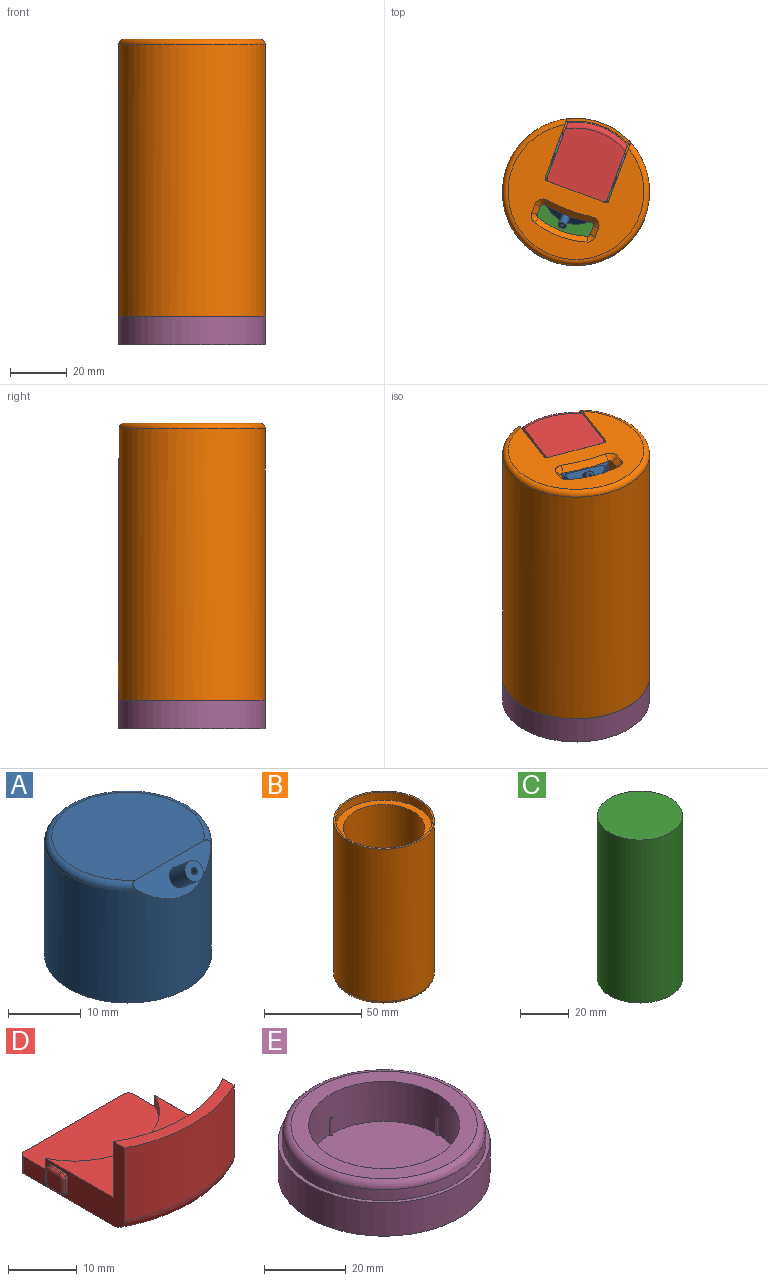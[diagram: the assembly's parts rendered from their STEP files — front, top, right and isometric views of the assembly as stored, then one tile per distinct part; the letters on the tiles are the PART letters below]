
ASSEMBLY  parts=5 mates=5
PART A: 32 faces, bbox 24.9x26.3x21.7 mm
  f0: cylinder r=1.6mm len=8mm, axis (0,0,-1), area 62.1mm2, adj f7,f15,f16,f17,f18,f19,f28
  f1: cylinder r=10.5mm len=21mm, axis (0,0,-1), area 1198.2mm2, adj f2,f3,f10,f12,f13,f20,f21,f22
  f2: plane 18.13x9.5mm, normal (0,0,-1), area 130.4mm2, adj f1,f6,f13,f21,f26
  f3: plane 5.66x3.24mm, normal (0,0.77,-0.64), area 15.1mm2, adj f1,f12,f25
  f4: cylinder r=1.5mm len=3.46mm, axis (0,-0.77,0.64), area 10.5mm2, adj f5,f6,f23,f24,f27
  f5: cylinder r=3mm len=0.33mm, axis (0,0,1), area 0mm2, adj f4,f6,f24
  f6: cylinder r=3mm len=15mm, axis (0,0,1), area 246.3mm2, adj f2,f4,f5,f12,f14,f20,f21,f22
  f7: plane 2x0.35mm, normal (0,0,-1), area 0.5mm2, adj f0,f18
  f8: cylinder r=11.5mm len=23mm, axis (0,0,-1), area 1342.1mm2, adj f10,f11,f29
  f9: plane 21x18.64mm, normal (0,0,1), area 325mm2, adj f11,f29
  f10: plane 23x23mm, normal (0,0,-1), area 69.1mm2, adj f1,f8
  f11: plane 14.95x4mm, normal (0,-0.77,0.64), area 50.5mm2, adj f8,f9,f29,f30
  f12: plane 18.13x9.5mm, normal (0,0,-1), area 130.4mm2, adj f1,f3,f6,f20,f25
  f13: plane 5.66x3.24mm, normal (0,0.77,-0.64), area 15.1mm2, adj f1,f2,f26
  f14: plane 6x6mm, normal (0,0,-1), area 7mm2, adj f6,f16
  f15: plane 2x0.35mm, normal (0,0,-1), area 0.5mm2, adj f0,f17
  f16: cone r=1.6mm half-angle=45deg, axis (0,0,-1), area 18.7mm2, adj f0,f14
  f17: plane 4x2mm, normal (-1,0,0), area 8mm2, adj f0,f15,f19
  f18: plane 4x2mm, normal (1,0,0), area 8mm2, adj f0,f7,f19
  f19: plane 3.2x2.5mm, normal (0,0,-1), area 7.1mm2, adj f0,f17,f18
  f20: plane 7.62x5mm, normal (-1,0,0), area 38.1mm2, adj f1,f6,f12,f22
  f21: plane 7.62x5mm, normal (1,0,0), area 38.1mm2, adj f1,f2,f6,f22
  f22: plane 7.67x2mm, normal (0,0,-1), area 15.1mm2, adj f1,f6,f20,f21
  f23: plane 0.4x0.02mm, normal (0,0,-1), area 0mm2, adj f4,f6,f25
  f24: plane 0.4x0.02mm, normal (0,0,-1), area 0mm2, adj f4,f5,f26
  f25: plane 7.79x6.72mm, normal (-1,0,0), area 48mm2, adj f1,f3,f6,f12,f23,f27
  f26: plane 7.79x6.72mm, normal (1,0,0), area 48mm2, adj f1,f2,f6,f13,f24,f27
  f27: plane 7.5x3mm, normal (0,0,-1), area 16.9mm2, adj f1,f4,f25,f26
  f28: cylinder r=0.5mm len=12.25mm, axis (0,-0.77,0.64), area 46.4mm2, adj f0,f31
  f29: torus R=10.5mm, axis (0,0,1), area 85.1mm2, adj f8,f9,f11
  f30: cylinder r=1.5mm len=4.99mm, axis (0,0.77,-0.64), area 37.7mm2, adj f11,f31
  f31: plane 3x2.3mm, normal (0,-0.77,0.64), area 6.3mm2, adj f28,f30
PART B: 56 faces, bbox 56.3x54.1x98 mm
  f0: plane 42x36.65mm, normal (0,0,1), area 733.9mm2, adj f1,f10,f11,f12,f16,f19,f29,f31
  f1: cylinder r=21mm len=91mm, axis (0,0,1), area 11675.7mm2, adj f0,f2,f8,f16,f17,f29,f30,f46
  f2: plane 22x4.11mm, normal (0,0,-1), area 23.1mm2, adj f1,f14,f46,f47
  f3: cylinder r=26mm len=96mm, axis (0,0,-1), area 15408.9mm2, adj f4,f6,f9,f10,f11,f42,f43
  f4: torus R=24mm, axis (0,0,1), area 420.3mm2, adj f3,f5,f10,f11
  f5: plane 48x44.78mm, normal (0,0,-1), area 1037.7mm2, adj f4,f10,f11,f12,f44,f45,f48,f49
  f6: plane 52x52mm, normal (0,0,1), area 160.2mm2, adj f3,f7
  f7: cylinder r=25mm len=50mm, axis (0,0,1), area 785.4mm2, adj f6,f8
  f8: plane 50x50mm, normal (0,0,1), area 578.1mm2, adj f1,f7
  f9: plane 22x3.55mm, normal (0,0,-1), area 22.7mm2, adj f3,f13,f42,f43
  f10: plane 23.07x18mm, normal (-1,0,0), area 253.9mm2, adj f0,f3,f4,f5,f13,f14,f15,f30
  f11: plane 23.07x18mm, normal (1,0,0), area 253.9mm2, adj f0,f3,f4,f5,f13,f14,f15,f17
  f12: plane 22x2mm, normal (0,1,0), area 44mm2, adj f0,f5,f44,f45
  f13: cylinder r=25mm len=24mm, axis (0,0,-1), area 125.7mm2, adj f9,f10,f11,f15,f42,f43
  f14: cylinder r=22mm len=24mm, axis (0,0,-1), area 127.4mm2, adj f2,f10,f11,f15,f46,f47
  f15: plane 24x6.56mm, normal (0,0,-1), area 75.6mm2, adj f10,f11,f13,f14
  f16: plane 15.65x10mm, normal (-1,0,0), area 142.8mm2, adj f0,f1,f17,f18,f19
  f17: plane 9.23x2mm, normal (0,0,1), area 17mm2, adj f1,f11,f16,f18
  f18: cylinder r=8mm len=8mm, axis (1,0,0), area 25.1mm2, adj f11,f16,f17,f19
  f19: plane 2x2mm, normal (0,-1,0), area 4mm2, adj f0,f11,f16,f18
  f20: plane 2x0.5mm, normal (0,0,-1), area 1mm2, adj f11,f21,f27,f28
  f21: cylinder r=1mm len=1mm, axis (1,0,0), area 0.8mm2, adj f11,f20,f22,f28
  f22: plane 5x0.5mm, normal (0,1,0), area 2.5mm2, adj f11,f21,f23,f28
  f23: cylinder r=1mm len=1mm, axis (1,0,0), area 0.8mm2, adj f11,f22,f24,f28
  f24: plane 2x0.5mm, normal (0,0,1), area 1mm2, adj f11,f23,f25,f28
  f25: cylinder r=1mm len=1mm, axis (1,0,0), area 0.8mm2, adj f11,f24,f26,f28
  f26: plane 5x0.5mm, normal (0,-1,0), area 2.5mm2, adj f11,f25,f27,f28
  f27: cylinder r=1mm len=1mm, axis (1,0,0), area 0.8mm2, adj f11,f20,f26,f28
  f28: plane 7x4mm, normal (1,0,0), area 27.1mm2, adj f20,f21,f22,f23,f24,f25,f26,f27
  f29: plane 15.65x10mm, normal (1,0,0), area 142.8mm2, adj f0,f1,f30,f31,f32
  f30: plane 9.23x2mm, normal (0,0,1), area 17mm2, adj f1,f10,f29,f32
  f31: plane 2x2mm, normal (0,-1,0), area 4mm2, adj f0,f10,f29,f32
  f32: cylinder r=8mm len=8mm, axis (-1,0,0), area 25.1mm2, adj f10,f29,f30,f31
  f33: plane 2x0.5mm, normal (0,0,-1), area 1mm2, adj f10,f34,f40,f41
  f34: cylinder r=1mm len=1mm, axis (-1,0,0), area 0.8mm2, adj f10,f33,f35,f41
  f35: plane 5x0.5mm, normal (0,-1,0), area 2.5mm2, adj f10,f34,f36,f41
  f36: cylinder r=1mm len=1mm, axis (-1,0,0), area 0.8mm2, adj f10,f35,f37,f41
  f37: plane 2x0.5mm, normal (0,0,1), area 1mm2, adj f10,f36,f38,f41
  f38: cylinder r=1mm len=1mm, axis (-1,0,0), area 0.8mm2, adj f10,f37,f39,f41
  f39: plane 5x0.5mm, normal (0,1,0), area 2.5mm2, adj f10,f38,f40,f41
  f40: cylinder r=1mm len=1mm, axis (-1,0,0), area 0.8mm2, adj f10,f33,f39,f41
  f41: plane 7x4mm, normal (-1,0,0), area 27.1mm2, adj f33,f34,f35,f36,f37,f38,f39,f40
  f42: cylinder r=1mm len=1.63mm, axis (0,1,0), area 1.8mm2, adj f3,f9,f11,f13
  f43: cylinder r=1mm len=1.63mm, axis (0,-1,0), area 1.8mm2, adj f3,f9,f10,f13
  f44: cylinder r=1mm len=2mm, axis (0,0,-1), area 3.1mm2, adj f0,f5,f11,f12
  f45: cylinder r=1mm len=2mm, axis (0,0,1), area 3.1mm2, adj f0,f5,f10,f12
  f46: cylinder r=1mm len=1.82mm, axis (0,-1,0), area 1.9mm2, adj f1,f2,f10,f14
  f47: cylinder r=1mm len=1.82mm, axis (0,1,0), area 1.9mm2, adj f1,f2,f11,f14
  f48: cone r=30mm half-angle=45deg, axis (0,0,-1), area 55.3mm2, adj f0,f5,f49,f50
  f49: cone r=1mm half-angle=45deg, axis (0,0,-1), area 7.1mm2, adj f0,f5,f48,f51
  f50: cone r=1mm half-angle=45deg, axis (0,0,-1), area 7.1mm2, adj f0,f5,f48,f52
  f51: plane 3.11x2mm, normal (-0.71,0,-0.71), area 8.8mm2, adj f0,f5,f49,f53
  f52: plane 3.11x2mm, normal (0.71,0,-0.71), area 8.8mm2, adj f0,f5,f50,f54
  f53: cone r=1mm half-angle=45deg, axis (0,0,-1), area 9.7mm2, adj f0,f5,f51,f55
  f54: cone r=1mm half-angle=45deg, axis (0,0,-1), area 9.7mm2, adj f0,f5,f52,f55
  f55: cone r=58mm half-angle=45deg, axis (0,0,1), area 49.4mm2, adj f0,f5,f53,f54
PART C: 3 faces, bbox 35x35x82 mm
  f0: cylinder r=17.5mm len=82mm, axis (0,0,-1), area 9016.4mm2, adj f1,f2
  f1: plane 35x35mm, normal (0,0,1), area 962.1mm2, adj f0
  f2: plane 35x35mm, normal (0,0,-1), area 962.1mm2, adj f0
PART D: 47 faces, bbox 26.6x26.5x15 mm
  f0: plane 20.54x3mm, normal (0,1,0), area 61.6mm2, adj f5,f8,f45,f46
  f1: plane 20.75x15mm, normal (-1,0,0), area 101.6mm2, adj f3,f4,f5,f6,f7,f8,f9,f10
  f2: plane 20.75x15mm, normal (1,0,0), area 101.6mm2, adj f3,f4,f5,f6,f7,f8,f9,f27
  f3: cylinder r=24.5mm len=22.54mm, axis (0,0,-1), area 304.5mm2, adj f1,f2,f4,f44
  f4: plane 22.54x5.03mm, normal (0,0,1), area 47mm2, adj f1,f2,f3,f6
  f5: plane 22.54x22.5mm, normal (0,0,-1), area 484.6mm2, adj f0,f1,f2,f44,f45,f46
  f6: cylinder r=22.5mm len=22.54mm, axis (0,0,-1), area 236.1mm2, adj f1,f2,f4,f7
  f7: plane 22.54x17.09mm, normal (0,0,1), area 248.6mm2, adj f1,f2,f6,f9
  f8: plane 22.54x12.5mm, normal (0,0,1), area 236mm2, adj f0,f1,f2,f9,f45,f46
  f9: cylinder r=12.5mm len=22.54mm, axis (0,0,1), area 56.2mm2, adj f1,f2,f7,f8
  f10: plane 2x0.34mm, normal (-0.09,-1,0), area 0.7mm2, adj f1,f11,f17,f22
  f11: cone r=1mm half-angle=5deg, axis (1,0,0), area 0.5mm2, adj f1,f10,f12,f20
  f12: plane 2x0.34mm, normal (-0.09,0,1), area 0.7mm2, adj f1,f11,f13,f19
  f13: cone r=1mm half-angle=5deg, axis (1,0,0), area 0.5mm2, adj f1,f12,f14,f21
  f14: plane 2x0.34mm, normal (-0.09,1,0), area 0.7mm2, adj f1,f13,f15,f23
  f15: cone r=1mm half-angle=5deg, axis (1,0,0), area 0.5mm2, adj f1,f14,f16,f25
  f16: plane 2x0.34mm, normal (-0.09,0,-1), area 0.7mm2, adj f1,f15,f17,f26
  f17: cone r=1mm half-angle=5deg, axis (1,0,0), area 0.5mm2, adj f1,f10,f16,f24
  f18: plane 2.94x2.94mm, normal (-1,0,0), area 8.5mm2, adj f19,f20,f21,f22,f23,f24,f25,f26
  f19: cylinder r=0.5mm len=2mm, axis (0,1,0), area 1.5mm2, adj f12,f18,f20,f21
  f20: torus R=0.47mm, axis (-1,0,0), area 0.9mm2, adj f11,f18,f19,f22
  f21: torus R=0.47mm, axis (-1,0,0), area 0.9mm2, adj f13,f18,f19,f23
  f22: cylinder r=0.5mm len=2mm, axis (0,0,1), area 1.5mm2, adj f10,f18,f20,f24
  f23: cylinder r=0.5mm len=2mm, axis (0,0,1), area 1.5mm2, adj f14,f18,f21,f25
  f24: torus R=0.47mm, axis (-1,0,0), area 0.9mm2, adj f17,f18,f22,f26
  f25: torus R=0.47mm, axis (-1,0,0), area 0.9mm2, adj f15,f18,f23,f26
  f26: cylinder r=0.5mm len=2mm, axis (0,1,0), area 1.5mm2, adj f16,f18,f24,f25
  f27: plane 2x0.34mm, normal (0.09,-1,0), area 0.7mm2, adj f2,f28,f34,f39
  f28: cone r=1mm half-angle=5deg, axis (-1,0,0), area 0.5mm2, adj f2,f27,f29,f41
  f29: plane 2x0.34mm, normal (0.09,0,-1), area 0.7mm2, adj f2,f28,f30,f43
  f30: cone r=1mm half-angle=5deg, axis (-1,0,0), area 0.5mm2, adj f2,f29,f31,f42
  f31: plane 2x0.34mm, normal (0.09,1,0), area 0.7mm2, adj f2,f30,f32,f40
  f32: cone r=1mm half-angle=5deg, axis (-1,0,0), area 0.5mm2, adj f2,f31,f33,f38
  f33: plane 2x0.34mm, normal (0.09,0,1), area 0.7mm2, adj f2,f32,f34,f36
  f34: cone r=1mm half-angle=5deg, axis (-1,0,0), area 0.5mm2, adj f2,f27,f33,f37
  f35: plane 2.94x2.94mm, normal (1,0,0), area 8.5mm2, adj f36,f37,f38,f39,f40,f41,f42,f43
  f36: cylinder r=0.5mm len=2mm, axis (0,1,0), area 1.5mm2, adj f33,f35,f37,f38
  f37: torus R=0.47mm, axis (1,0,0), area 0.9mm2, adj f34,f35,f36,f39
  f38: torus R=0.47mm, axis (1,0,0), area 0.9mm2, adj f32,f35,f36,f40
  f39: cylinder r=0.5mm len=2mm, axis (0,0,1), area 1.5mm2, adj f27,f35,f37,f41
  f40: cylinder r=0.5mm len=2mm, axis (0,0,1), area 1.5mm2, adj f31,f35,f38,f42
  f41: torus R=0.47mm, axis (1,0,0), area 0.9mm2, adj f28,f35,f39,f43
  f42: torus R=0.47mm, axis (1,0,0), area 0.9mm2, adj f30,f35,f40,f43
  f43: cylinder r=0.5mm len=2mm, axis (0,1,0), area 1.5mm2, adj f29,f35,f41,f42
  f44: torus R=22.5mm, axis (0,0,1), area 73.8mm2, adj f1,f2,f3,f5
  f45: cylinder r=1mm len=3mm, axis (0,0,1), area 4.7mm2, adj f0,f2,f5,f8
  f46: cylinder r=1mm len=3mm, axis (0,0,-1), area 4.7mm2, adj f0,f1,f5,f8
PART E: 16 faces, bbox 53.8x53.8x15 mm
  f0: cylinder r=18.5mm len=37mm, axis (0,0,1), area 1374.9mm2, adj f1,f6,f8,f9,f10,f11,f12,f13
  f1: plane 36.99x36.99mm, normal (0,0,1), area 1073.6mm2, adj f0,f8,f10,f12,f14
  f2: cylinder r=26mm len=52mm, axis (0,0,-1), area 1633.6mm2, adj f3,f4
  f3: plane 52x52mm, normal (0,0,1), area 160.2mm2, adj f2,f5
  f4: plane 52x52mm, normal (0,0,-1), area 2123.7mm2, adj f2
  f5: cone r=25mm half-angle=3deg, axis (0,0,-1), area 486.8mm2, adj f3,f7
  f6: plane 45.68x45.68mm, normal (0,0,1), area 563.7mm2, adj f0,f7
  f7: torus R=22.84mm, axis (0,0,1), area 459.6mm2, adj f5,f6
  f8: cylinder r=0.5mm len=5mm, axis (0,0,-1), area 7.8mm2, adj f0,f1,f9
  f9: plane 1x0.5mm, normal (0,0,1), area 0.4mm2, adj f0,f8
  f10: cylinder r=0.5mm len=5mm, axis (0,0,-1), area 7.8mm2, adj f0,f1,f11
  f11: plane 1x0.5mm, normal (0,0,1), area 0.4mm2, adj f0,f10
  f12: cylinder r=0.5mm len=5mm, axis (0,0,-1), area 7.8mm2, adj f0,f1,f13
  f13: plane 1x0.5mm, normal (0,0,1), area 0.4mm2, adj f0,f12
  f14: cylinder r=0.5mm len=5mm, axis (0,0,-1), area 7.8mm2, adj f0,f1,f15
  f15: plane 1x0.5mm, normal (0,0,1), area 0.4mm2, adj f0,f14
PLACE A rot(axis=(0,0,-1),22.4deg) t=(0,0,85)mm
PLACE B rot(axis=(-0.18,-0.98,0),180deg) t=(0,0,108)mm
PLACE C t=(0,0,3)mm
PLACE D rot(axis=(-0.98,0.18,0),180deg) t=(2.32,6.19,108)mm
PLACE E at identity
MATE revolute C.f0 <-> E.f0  axis (0,0,-1) through (0,0,3)mm
MATE planar D.f3 <-> B.f3  axis (0,0,1) through (0,0,108)mm
MATE revolute B.f3 <-> E.f2  axis (0,0,-1) through (0,0,10)mm
MATE slider B.f14 <-> D.f3  axis (0,0,1) through (0,0,93.02)mm
MATE revolute C.f0 <-> A.f1  axis (0,0,1) through (0,0,85)mm
